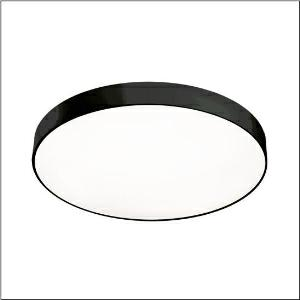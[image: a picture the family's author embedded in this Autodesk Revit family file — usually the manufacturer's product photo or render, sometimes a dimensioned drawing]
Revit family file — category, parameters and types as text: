
# Revit family: round_21_l_51mr38fd0421b
name_source: partatom
category: Lighting Fixtures
units: mm (PartAtom-declared; Revit-internal decimal feet)

## family parameters
Cut with Voids When Loaded = No
Host = Face
Light Source = No
Part Type = Normal
Room Calculation Point = No
Round Connector Dimension = Use Diameter
Shared = No

## types (1)
- Round 21 L (1 x LED, 13080 lm, 98.3 W, 4000K)
    Apparent Load = 98 VA
    CIE Flux Codes = 49 80 96 100 100
    Color Rendering = 80
    Color Temperature = 4000K
    Default Elevation = 1800 mm
    Description = Round 21 L, wall and ceiling luminaire, primary optical cover: cover, of PMMA, opal, light emission: direct distribution, primary light characteristic: symmetric, installation type: suspended mounting, surface-mounted, LED, rated luminous flux: 13.080lm, luminous efficacy: 133lm/W, light colour: 840, colour temperature: 4000K, with terminal, 5-pole, mains connection: 230V, AC, 50/60Hz, rated input power: 98W, housing, of aluminium, coated, black, diameter: 850mm, height: 62mm, protection rating (complete): IP40, insulation class (complete): insulation class I (protective earthing), certification: CE, impact resistance: IK04, permissible operating ambient temperature: -10..+35°C, packaging unit: 1 piece
    Height = 87 mm
    Lamp = 1 x LED
    Lamp Light Flux = 13080 lm
    Lamp Power = 98.3 W
    Lamp count = 1
    Length = 850 mm
    Luminous efficacy = 133 lm/W
    Manufacturer = Siteco
    ModVariant = No
    Model = 51MR38FD0421B
    Mounting Place = Ceiling
    Mounting Type = Surface mounted
    Number of Poles = 1
    OnlyDefault = Yes
    Power Factor = 1
    Product Name = Round 21 L
    Product group = wall and ceiling luminaire
    ProductGroupID = 302
    Protection Class = Protection class I
    Protection Degree = IP 40
    RLX_Detail_Level = 1
    RLX_Emergency_Light_Flux = 0 lm
    RLX_Emergency_Type = 0
    RLX_Emergency_Type_DB = No
    RlxData = <blob elided: 23889 chars, md5=748014c9>
    Socket = socket
    Standby Power = 0 W
    System Light Flux = 13080 lm
    System Power = 98 W
    Type Comments = Product without accessories
    Type Image = l_1258328.jpg
    URL = http://relux.com
    VarID = ---
    Voltage = 0 V
    Weight = 0.00 kg
    Width = 0 mm  [stored 0 ft]

note: [stored X ft] marks values corroborated as IEEE doubles in the binary element streams (Revit-internal decimal feet)

## geometry (parser evidence)
native form markers: Blend x4, Sweep x13
no freeform markers — native parametric forms only
